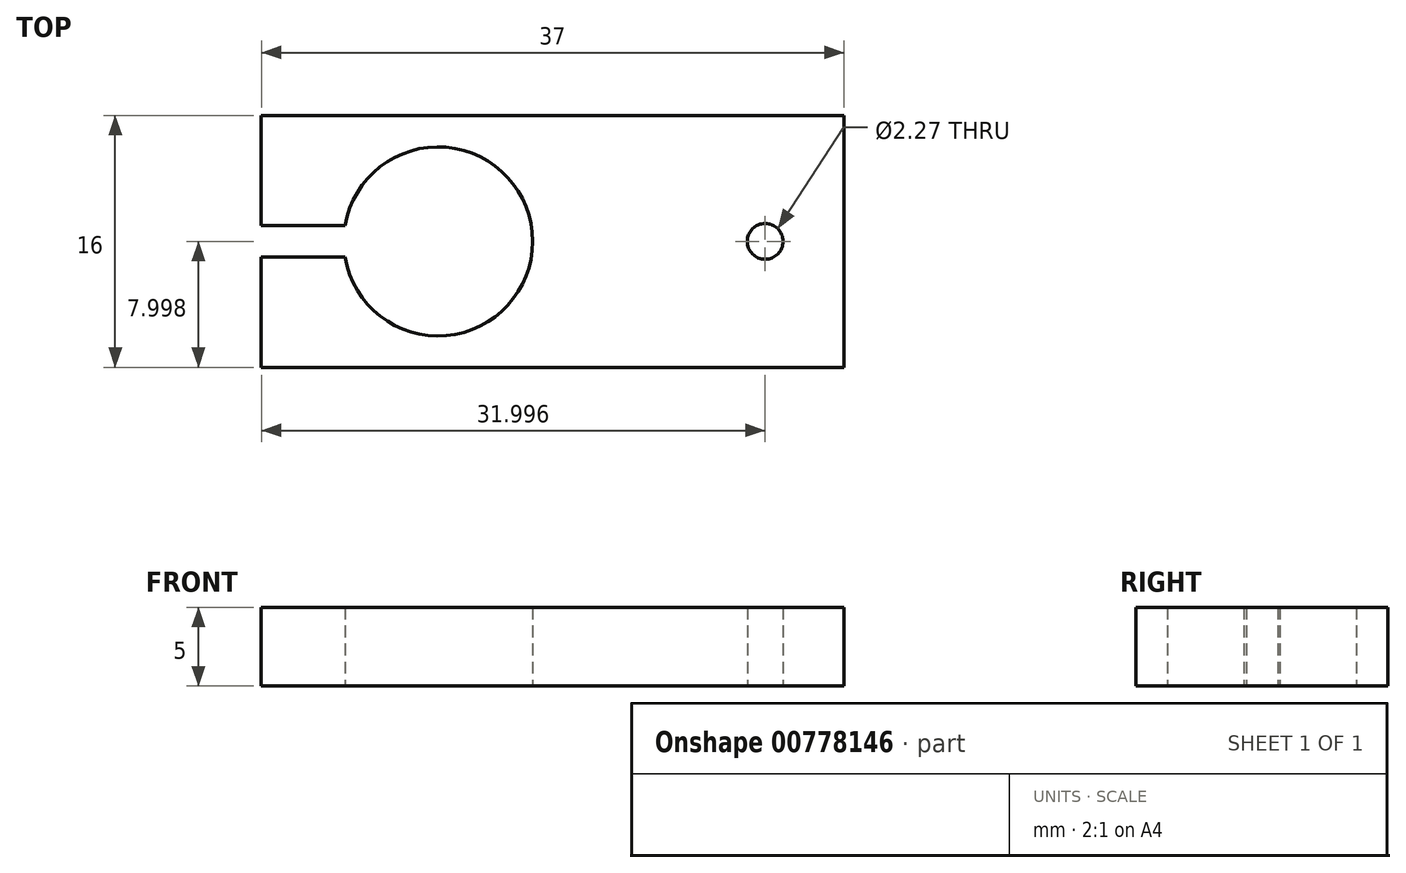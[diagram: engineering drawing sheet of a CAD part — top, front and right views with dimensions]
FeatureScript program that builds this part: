
annotation { "Feature Type Name" : "Feature", "Feature Type Description" : "" }
export const myFeature = defineFeature(function(context is Context, id is Id, definition is map)
    precondition{}
    {
        {
            var Q0;
            Q0=qCreatedBy(makeId("Top.planeOp"),FACE);
            var sketch = newSketch(context, id + "F0", { "sketchPlane" : qUnion([Q0])});
            skLineSegment(sketch, "E0.bottom", {"start": v(-61.08, -54.86) * mm, "end": v(-24.08, -54.86) * mm});
            skLineSegment(sketch, "E0.top", {"start": v(-61.08, -70.86) * mm, "end": v(-24.08, -70.86) * mm});
            skLineSegment(sketch, "E0.left", {"start": v(-61.08, -54.86) * mm, "end": v(-61.08, -61.86) * mm});
            skLineSegment(sketch, "E0.right", {"start": v(-24.08, -54.86) * mm, "end": v(-24.08, -70.86) * mm});
            skArc(sketch, "E1", {"start": v(-55.77, -63.86) * mm, "mid": v(-43.85, -62.86) * mm, "end": v(-55.77, -61.86) * mm});
            skPoint(sketch, "E1.centerSnap0", {"position": v(-61.08, -62.86) * mm});
            skCircle(sketch, "E2", {"center": v(-29.08, -62.86) * mm, "radius": 1.14 * mm});
            skLineSegment(sketch, "E3", {"start": v(-61.08, -61.86) * mm, "end": v(-55.77, -61.86) * mm});
            skLineSegment(sketch, "E4", {"start": v(-61.08, -63.86) * mm, "end": v(-55.77, -63.86) * mm});
            skLineSegment(sketch, "E5.trimOffspring", {"start": v(-61.08, -63.86) * mm, "end": v(-61.08, -70.86) * mm});
            skSolve(sketch);
        }
        {
            var Q0;
            {var subQ1=sQuery(id+"F0.wireOp",EDGE,"E0.bottom");Q0=makeQuery(id+"F0.imprint","IMPRINT",FACE,{"disambiguationData":[TD([[makeQuery(id+"F0.imprint","IMPRINT",EDGE,{"derivedFrom":subQ1}),-1.0]])]});}
            extrude(context, id + "F1", {"entities" : qUnion([Q0]), "depth" : 5 * mm, "offsetDistance" : 25 * mm});
        }
    });
